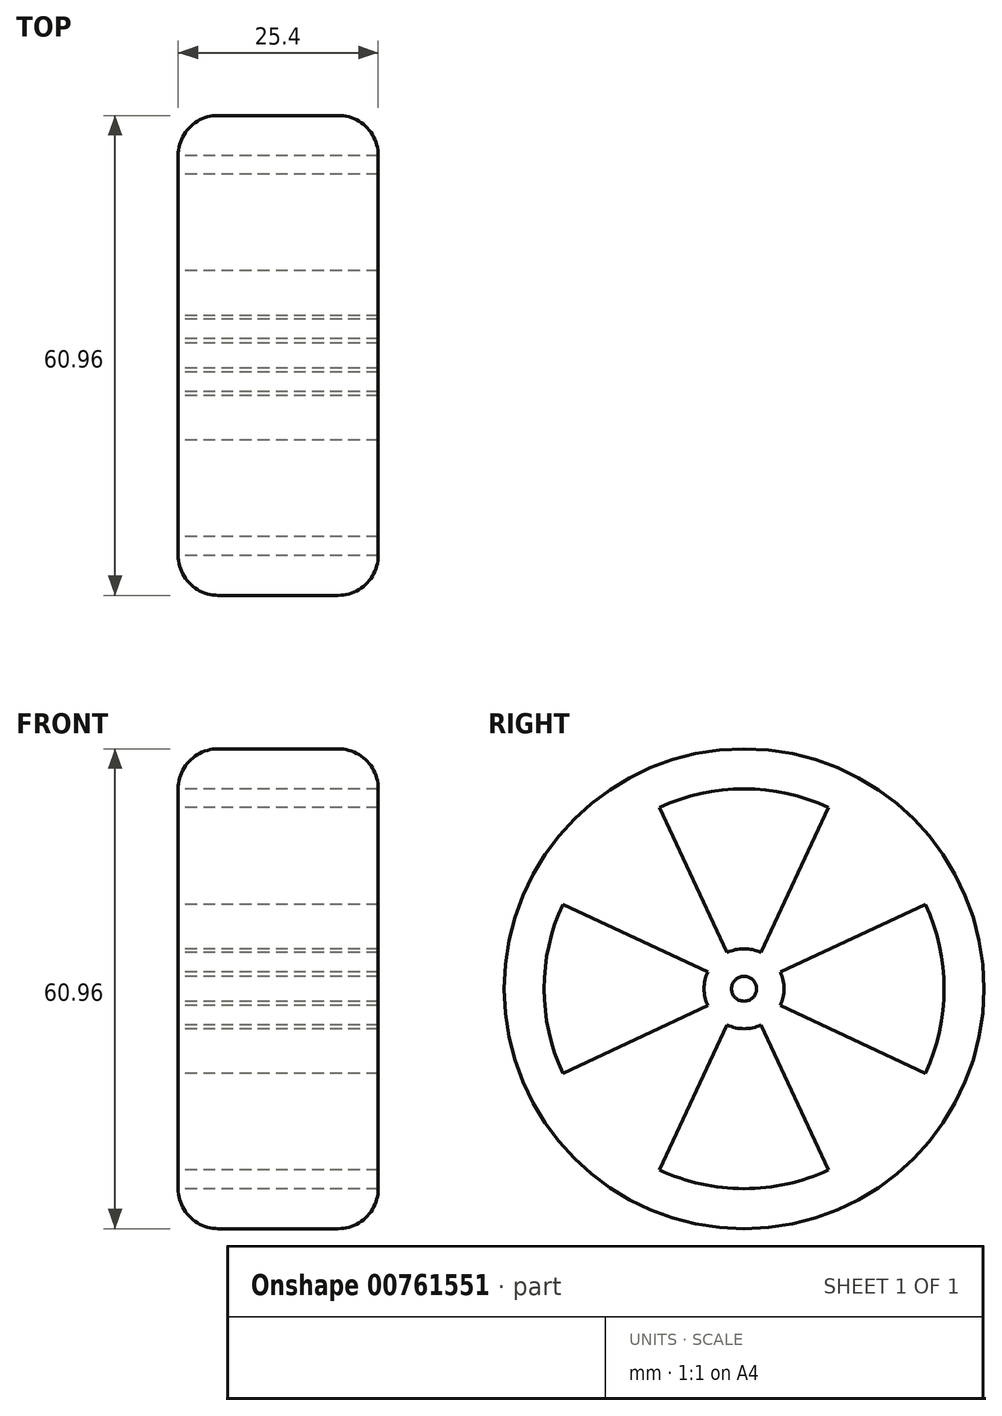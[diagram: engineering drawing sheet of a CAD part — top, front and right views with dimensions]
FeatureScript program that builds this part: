
annotation { "Feature Type Name" : "Feature", "Feature Type Description" : "" }
export const myFeature = defineFeature(function(context is Context, id is Id, definition is map)
    precondition{}
    {
        {
            var Q0;
            Q0=qCreatedBy(makeId("Right.planeOp"),FACE);
            var sketch = newSketch(context, id + "F0", { "sketchPlane" : qUnion([Q0])});
            skCircle(sketch, "E0", {"center": v(0, 0) * mm, "radius": 30.48 * mm});
            skCircle(sketch, "E1.0", {"center": v(0, 0) * mm, "radius": 25.4 * mm});
            skCircle(sketch, "E2", {"center": v(0, 0) * mm, "radius": 1.59 * mm});
            skLineSegment(sketch, "E3", {"start": v(0, 1.59) * mm, "end": v(0, 25.4) * mm});
            skLineSegment(sketch, "E4", {"start": v(0, 25.4) * mm, "end": v(0, 1.59) * mm});
            skLineSegment(sketch, "E5", {"start": v(0, -25.4) * mm, "end": v(0, -1.59) * mm});
            skLineSegment(sketch, "E6", {"start": v(25.4, 0) * mm, "end": v(1.59, 0) * mm});
            skLineSegment(sketch, "E7", {"start": v(-25.4, 0) * mm, "end": v(-1.59, 0) * mm});
            skLineSegment(sketch, "E8", {"start": v(0.67, 1.44) * mm, "end": v(10.73, 23.02) * mm});
            skLineSegment(sketch, "E9", {"start": v(1.44, 0.67) * mm, "end": v(23.02, 10.73) * mm});
            skLineSegment(sketch, "E10", {"start": v(1.44, -0.67) * mm, "end": v(23.02, -10.73) * mm});
            skLineSegment(sketch, "E11", {"start": v(0.67, -1.44) * mm, "end": v(10.73, -23.02) * mm});
            skLineSegment(sketch, "E12", {"start": v(-0.67, -1.44) * mm, "end": v(-10.73, -23.02) * mm});
            skLineSegment(sketch, "E13", {"start": v(-1.44, -0.67) * mm, "end": v(-23.02, -10.73) * mm});
            skLineSegment(sketch, "E14", {"start": v(-0.67, 1.44) * mm, "end": v(-10.73, 23.02) * mm});
            skLineSegment(sketch, "E15", {"start": v(-1.44, 0.67) * mm, "end": v(-23.02, 10.73) * mm});
            skLineSegment(sketch, "E16.trimOffspring", {"start": v(0, -1.59) * mm, "end": v(0, -25.4) * mm});
            skLineSegment(sketch, "E17.trimOffspring", {"start": v(1.59, 0) * mm, "end": v(25.4, 0) * mm});
            skLineSegment(sketch, "E18.trimOffspring", {"start": v(-1.59, 0) * mm, "end": v(-25.4, 0) * mm});
            skCircle(sketch, "E19", {"center": v(0, 0) * mm, "radius": 5.08 * mm});
            skSolve(sketch);
        }
        {
            var Q0;
            Q0 = qSketchRegion(id + "F0", true);
            var Q1;
            {var subQ0=sQuery(id+"F0.wireOp",EDGE,"E8");var subQ1=sQuery(id+"F0.wireOp",EDGE,"E1.0");var subQ2=makeQuery(id+"F0.imprint","INTERSECT",VERTEX,{"derivedFrom":[subQ1,subQ0]});Q1=makeQuery(id+"F0.imprint","IMPRINT",FACE,{"disambiguationData":[TD([[makeQuery(id+"F0.imprint","IMPRINT",EDGE,{"disambiguationData":[TD([[subQ2,1.0]])],"derivedFrom":subQ1}),1.0]])]});}
            var Q2;
            {var subQ0=sQuery(id+"F0.wireOp",EDGE,"E10");var subQ1=sQuery(id+"F0.wireOp",EDGE,"E1.0");var subQ2=makeQuery(id+"F0.imprint","INTERSECT",VERTEX,{"derivedFrom":[subQ1,subQ0]});Q2=makeQuery(id+"F0.imprint","IMPRINT",FACE,{"disambiguationData":[TD([[makeQuery(id+"F0.imprint","IMPRINT",EDGE,{"disambiguationData":[TD([[subQ2,1.0]])],"derivedFrom":subQ1}),1.0]])]});}
            var Q3;
            {var subQ0=sQuery(id+"F0.wireOp",EDGE,"E10");var subQ1=sQuery(id+"F0.wireOp",EDGE,"E2");var subQ2=makeQuery(id+"F0.imprint","INTERSECT",VERTEX,{"derivedFrom":[subQ1,subQ0]});Q3=makeQuery(id+"F0.imprint","IMPRINT",FACE,{"disambiguationData":[TD([[makeQuery(id+"F0.imprint","IMPRINT",EDGE,{"disambiguationData":[TD([[subQ2,1.0]])],"derivedFrom":subQ1}),-1.0]])]});}
            var Q4;
            {var subQ0=sQuery(id+"F0.wireOp",EDGE,"E10");var subQ1=sQuery(id+"F0.wireOp",EDGE,"E2");var subQ2=makeQuery(id+"F0.imprint","INTERSECT",VERTEX,{"derivedFrom":[subQ1,subQ0]});Q4=makeQuery(id+"F0.imprint","IMPRINT",FACE,{"disambiguationData":[TD([[makeQuery(id+"F0.imprint","IMPRINT",EDGE,{"disambiguationData":[TD([[subQ2,-1.0]])],"derivedFrom":subQ1}),-1.0]])]});}
            var Q5;
            {var subQ0=sQuery(id+"F0.wireOp",EDGE,"E9");var subQ1=sQuery(id+"F0.wireOp",EDGE,"E2");var subQ2=makeQuery(id+"F0.imprint","INTERSECT",VERTEX,{"derivedFrom":[subQ1,subQ0]});Q5=makeQuery(id+"F0.imprint","IMPRINT",FACE,{"disambiguationData":[TD([[makeQuery(id+"F0.imprint","IMPRINT",EDGE,{"disambiguationData":[TD([[subQ2,1.0]])],"derivedFrom":subQ1}),-1.0]])]});}
            var Q6;
            {var subQ0=sQuery(id+"F0.wireOp",EDGE,"E8");var subQ1=sQuery(id+"F0.wireOp",EDGE,"E2");var subQ2=makeQuery(id+"F0.imprint","INTERSECT",VERTEX,{"derivedFrom":[subQ1,subQ0]});Q6=makeQuery(id+"F0.imprint","IMPRINT",FACE,{"disambiguationData":[TD([[makeQuery(id+"F0.imprint","IMPRINT",EDGE,{"disambiguationData":[TD([[subQ2,1.0]])],"derivedFrom":subQ1}),-1.0]])]});}
            var Q7;
            {var subQ0=sQuery(id+"F0.wireOp",EDGE,"E4");var subQ1=sQuery(id+"F0.wireOp",EDGE,"E2");var subQ2=makeQuery(id+"F0.imprint","INTERSECT",VERTEX,{"derivedFrom":[subQ1,subQ0]});Q7=makeQuery(id+"F0.imprint","IMPRINT",FACE,{"disambiguationData":[TD([[makeQuery(id+"F0.imprint","IMPRINT",EDGE,{"disambiguationData":[TD([[subQ2,1.0]])],"derivedFrom":subQ1}),-1.0]])]});}
            var Q8;
            {var subQ0=sQuery(id+"F0.wireOp",EDGE,"E4");var subQ1=sQuery(id+"F0.wireOp",EDGE,"E2");var subQ2=makeQuery(id+"F0.imprint","INTERSECT",VERTEX,{"derivedFrom":[subQ1,subQ0]});Q8=makeQuery(id+"F0.imprint","IMPRINT",FACE,{"disambiguationData":[TD([[makeQuery(id+"F0.imprint","IMPRINT",EDGE,{"disambiguationData":[TD([[subQ2,-1.0]])],"derivedFrom":subQ1}),-1.0]])]});}
            var Q9;
            {var subQ0=sQuery(id+"F0.wireOp",EDGE,"E14");var subQ1=sQuery(id+"F0.wireOp",EDGE,"E2");var subQ2=makeQuery(id+"F0.imprint","INTERSECT",VERTEX,{"derivedFrom":[subQ1,subQ0]});Q9=makeQuery(id+"F0.imprint","IMPRINT",FACE,{"disambiguationData":[TD([[makeQuery(id+"F0.imprint","IMPRINT",EDGE,{"disambiguationData":[TD([[subQ2,-1.0]])],"derivedFrom":subQ1}),-1.0]])]});}
            var Q10;
            {var subQ0=sQuery(id+"F0.wireOp",EDGE,"E15");var subQ1=sQuery(id+"F0.wireOp",EDGE,"E2");var subQ2=makeQuery(id+"F0.imprint","INTERSECT",VERTEX,{"derivedFrom":[subQ1,subQ0]});Q10=makeQuery(id+"F0.imprint","IMPRINT",FACE,{"disambiguationData":[TD([[makeQuery(id+"F0.imprint","IMPRINT",EDGE,{"disambiguationData":[TD([[subQ2,-1.0]])],"derivedFrom":subQ1}),-1.0]])]});}
            var Q11;
            {var subQ0=sQuery(id+"F0.wireOp",EDGE,"E13");var subQ1=sQuery(id+"F0.wireOp",EDGE,"E2");var subQ2=makeQuery(id+"F0.imprint","INTERSECT",VERTEX,{"derivedFrom":[subQ1,subQ0]});Q11=makeQuery(id+"F0.imprint","IMPRINT",FACE,{"disambiguationData":[TD([[makeQuery(id+"F0.imprint","IMPRINT",EDGE,{"disambiguationData":[TD([[subQ2,1.0]])],"derivedFrom":subQ1}),-1.0]])]});}
            var Q12;
            {var subQ0=sQuery(id+"F0.wireOp",EDGE,"E12");var subQ1=sQuery(id+"F0.wireOp",EDGE,"E2");var subQ2=makeQuery(id+"F0.imprint","INTERSECT",VERTEX,{"derivedFrom":[subQ1,subQ0]});Q12=makeQuery(id+"F0.imprint","IMPRINT",FACE,{"disambiguationData":[TD([[makeQuery(id+"F0.imprint","IMPRINT",EDGE,{"disambiguationData":[TD([[subQ2,1.0]])],"derivedFrom":subQ1}),-1.0]])]});}
            var Q13;
            {var subQ0=sQuery(id+"F0.wireOp",EDGE,"E12");var subQ1=sQuery(id+"F0.wireOp",EDGE,"E2");var subQ2=makeQuery(id+"F0.imprint","INTERSECT",VERTEX,{"derivedFrom":[subQ1,subQ0]});Q13=makeQuery(id+"F0.imprint","IMPRINT",FACE,{"disambiguationData":[TD([[makeQuery(id+"F0.imprint","IMPRINT",EDGE,{"disambiguationData":[TD([[subQ2,-1.0]])],"derivedFrom":subQ1}),-1.0]])]});}
            var Q14;
            {var subQ0=sQuery(id+"F0.wireOp",EDGE,"E11");var subQ1=sQuery(id+"F0.wireOp",EDGE,"E2");var subQ2=makeQuery(id+"F0.imprint","INTERSECT",VERTEX,{"derivedFrom":[subQ1,subQ0]});Q14=makeQuery(id+"F0.imprint","IMPRINT",FACE,{"disambiguationData":[TD([[makeQuery(id+"F0.imprint","IMPRINT",EDGE,{"disambiguationData":[TD([[subQ2,1.0]])],"derivedFrom":subQ1}),-1.0]])]});}
            var Q15;
            {var subQ0=sQuery(id+"F0.wireOp",EDGE,"E14");var subQ1=sQuery(id+"F0.wireOp",EDGE,"E1.0");var subQ2=makeQuery(id+"F0.imprint","INTERSECT",VERTEX,{"derivedFrom":[subQ1,subQ0]});Q15=makeQuery(id+"F0.imprint","IMPRINT",FACE,{"disambiguationData":[TD([[makeQuery(id+"F0.imprint","IMPRINT",EDGE,{"disambiguationData":[TD([[subQ2,-1.0]])],"derivedFrom":subQ1}),1.0]])]});}
            var Q16;
            {var subQ0=sQuery(id+"F0.wireOp",EDGE,"E12");var subQ1=sQuery(id+"F0.wireOp",EDGE,"E1.0");var subQ2=makeQuery(id+"F0.imprint","INTERSECT",VERTEX,{"derivedFrom":[subQ1,subQ0]});Q16=makeQuery(id+"F0.imprint","IMPRINT",FACE,{"disambiguationData":[TD([[makeQuery(id+"F0.imprint","IMPRINT",EDGE,{"disambiguationData":[TD([[subQ2,1.0]])],"derivedFrom":subQ1}),1.0]])]});}
            extrude(context, id + "F1", {"entities" : qUnion([Q0, Q1, Q2, Q3, Q4, Q5, Q6, Q7, Q8, Q9, Q10, Q11, Q12, Q13, Q14, Q15, Q16]), "depth" : 25.4 * mm, "offsetDistance" : 25.4 * mm});
        }
        {
            var Q0;
            Q0=makeQuery(id+"F1.opExtrude","CAP_EDGE",EDGE,{"disambiguationData":[OSD([sQuery(id+"F0.wireOp",EDGE,"E0")])],"isStart":false});
            var Q1;
            Q1=makeQuery(id+"F1.opExtrude","CAP_EDGE",EDGE,{"disambiguationData":[OSD([sQuery(id+"F0.wireOp",EDGE,"E0")])],"isStart":true});
            fillet(context, id + "F2", {"entities" : qUnion([Q0, Q1]), "radius" : 5.08 * mm, "tangentPropagation" : true, "allowEdgeOverflow" : false});
        }
    });
